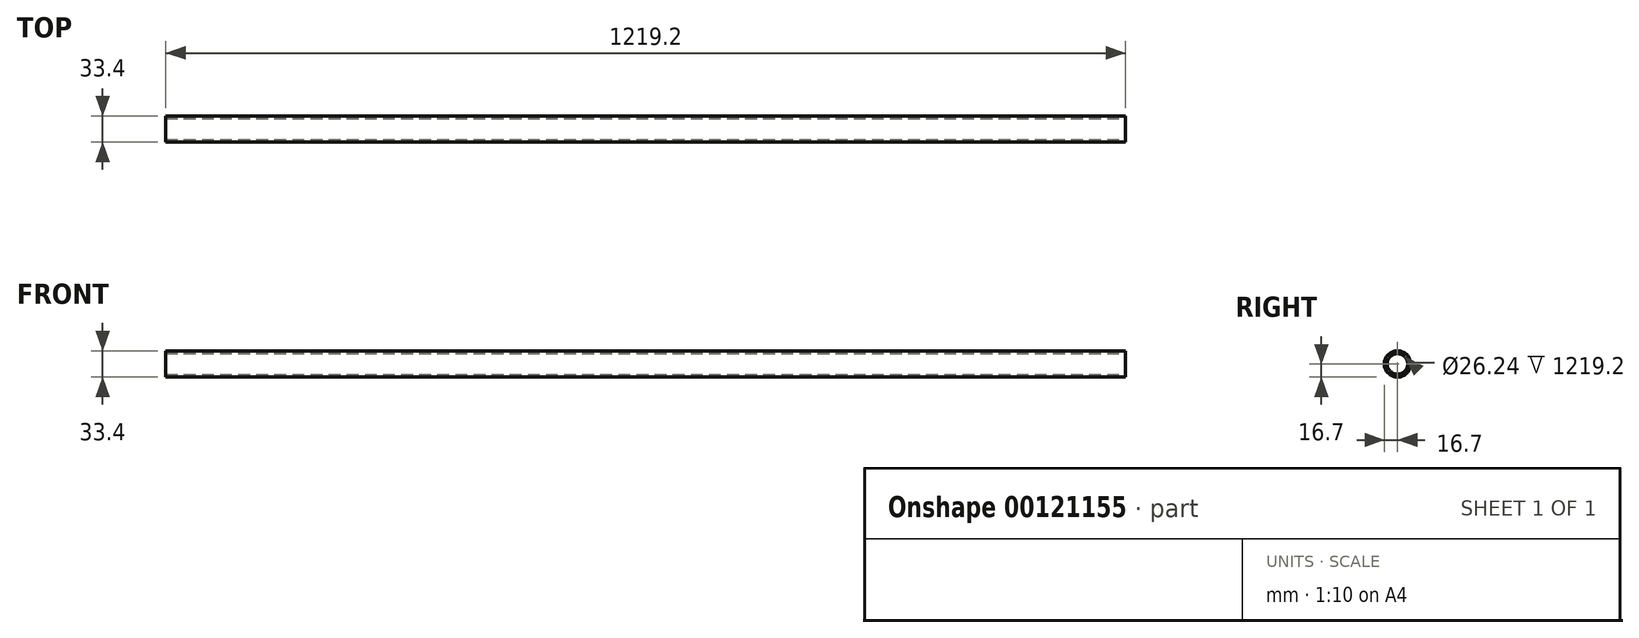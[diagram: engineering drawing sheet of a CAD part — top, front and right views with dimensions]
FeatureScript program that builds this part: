
annotation { "Feature Type Name" : "Feature", "Feature Type Description" : "" }
export const myFeature = defineFeature(function(context is Context, id is Id, definition is map)
    precondition{}
    {
        {
            var Q0;
            Q0=qCreatedBy(makeId("Right.planeOp"),FACE);
            var sketch = newSketch(context, id + "F0", { "sketchPlane" : qUnion([Q0])});
            skCircle(sketch, "E0", {"center": v(0, 0) * mm, "radius": 16.7 * mm});
            skCircle(sketch, "E1", {"center": v(0, 0) * mm, "radius": 13.12 * mm});
            skSolve(sketch);
        }
        {
            var Q0;
            Q0=makeQuery(id+"F0.imprint","IMPRINT",FACE,{"disambiguationData":[TD([[makeQuery(id+"F0.imprint","IMPRINT",EDGE,{"derivedFrom":sQuery(id+"F0.wireOp",EDGE,"E0")}),1.0]])]});
            extrude(context, id + "F1", {"entities" : qUnion([Q0]), "oppositeDirection" : true, "depth" : 1219.2 * mm});
        }
    });
